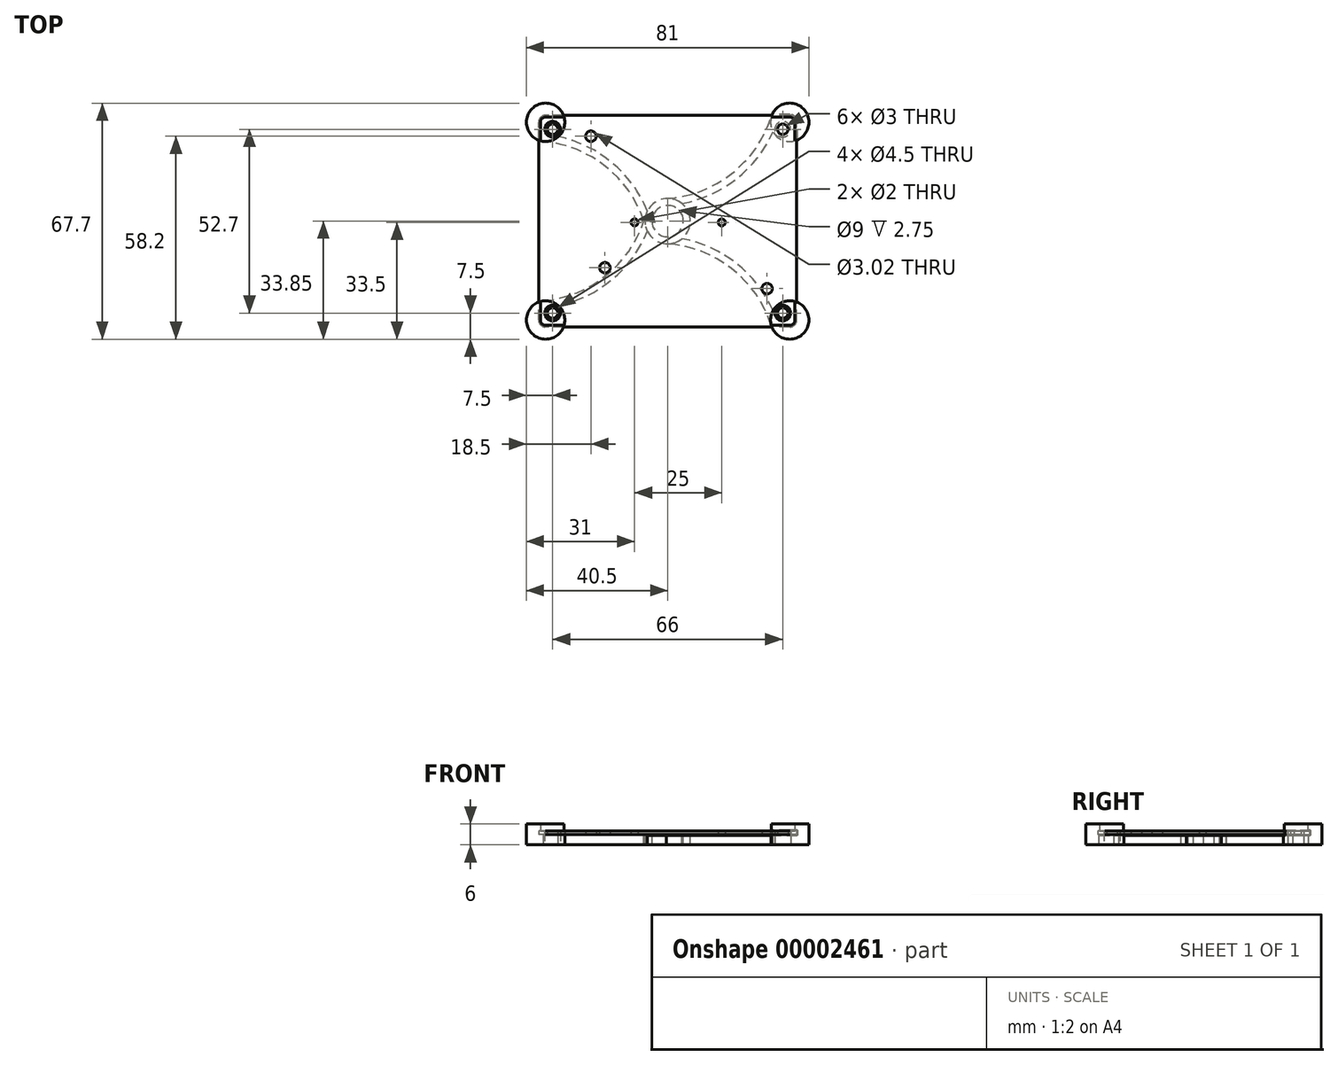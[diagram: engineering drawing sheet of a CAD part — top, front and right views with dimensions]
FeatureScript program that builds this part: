
annotation { "Feature Type Name" : "Feature", "Feature Type Description" : "" }
export const myFeature = defineFeature(function(context is Context, id is Id, definition is map)
    precondition{}
    {
        {
            var Q0;
            Q0=qCreatedBy(makeId("Top.planeOp"),FACE);
            var sketch = newSketch(context, id + "F0", { "sketchPlane" : qUnion([Q0])});
            skLineSegment(sketch, "E0.rect.bottom", {"start": v(35, -30.35) * mm, "end": v(-35, -30.35) * mm});
            skLineSegment(sketch, "E0.rect.top", {"start": v(35, 30.35) * mm, "end": v(-35, 30.35) * mm});
            skLineSegment(sketch, "E0.rect.left", {"start": v(37, -28.35) * mm, "end": v(37, 28.35) * mm});
            skLineSegment(sketch, "E0.rect.right", {"start": v(-37, -28.35) * mm, "end": v(-37, 28.35) * mm});
            skPoint(sketch, "E0.rect.middle", {"position": v(0, 0) * mm});
            skPoint(sketch, "E1.visualSharp", {"position": v(-37, 30.35) * mm});
            skArc(sketch, "E1.filletArc", {"start": v(-35, 30.35) * mm, "mid": v(-36.41, 29.76) * mm, "end": v(-37, 28.35) * mm});
            skPoint(sketch, "E2.visualSharp", {"position": v(37, 30.35) * mm});
            skArc(sketch, "E2.filletArc", {"start": v(37, 28.35) * mm, "mid": v(36.41, 29.76) * mm, "end": v(35, 30.35) * mm});
            skPoint(sketch, "E3.visualSharp", {"position": v(37, -30.35) * mm});
            skArc(sketch, "E3.filletArc", {"start": v(35, -30.35) * mm, "mid": v(36.41, -29.76) * mm, "end": v(37, -28.35) * mm});
            skPoint(sketch, "E4.visualSharp", {"position": v(-37, -30.35) * mm});
            skArc(sketch, "E4.filletArc", {"start": v(-37, -28.35) * mm, "mid": v(-36.41, -29.76) * mm, "end": v(-35, -30.35) * mm});
            skLineSegment(sketch, "E5.rect.bottom", {"start": v(33, -26.35) * mm, "end": v(-33, -26.35) * mm, "construction": true});
            skLineSegment(sketch, "E5.rect.top", {"start": v(33, 26.35) * mm, "end": v(-33, 26.35) * mm, "construction": true});
            skLineSegment(sketch, "E5.rect.left", {"start": v(33, -26.35) * mm, "end": v(33, 26.35) * mm, "construction": true});
            skLineSegment(sketch, "E5.rect.right", {"start": v(-33, -26.35) * mm, "end": v(-33, 26.35) * mm, "construction": true});
            skCircle(sketch, "E6", {"center": v(-33, 26.35) * mm, "radius": 1.5 * mm});
            skCircle(sketch, "E7", {"center": v(33, 26.35) * mm, "radius": 1.5 * mm});
            skCircle(sketch, "E8", {"center": v(33, -26.35) * mm, "radius": 1.5 * mm});
            skCircle(sketch, "E9", {"center": v(-33, -26.35) * mm, "radius": 1.5 * mm});
            skLineSegment(sketch, "E10", {"start": v(-33, 26.35) * mm, "end": v(0, 0) * mm, "construction": true});
            skLineSegment(sketch, "E11", {"start": v(33, 26.35) * mm, "end": v(0, 0) * mm, "construction": true});
            skCircle(sketch, "E12", {"center": v(-22, 24.35) * mm, "radius": 1.51 * mm});
            skCircle(sketch, "E13", {"center": v(-18, -13.35) * mm, "radius": 1.5 * mm});
            skCircle(sketch, "E14", {"center": v(28.5, -19.35) * mm, "radius": 1.5 * mm});
            skCircle(sketch, "E15", {"center": v(15.5, -0.35) * mm, "radius": 1 * mm});
            skCircle(sketch, "E16", {"center": v(-9.5, -0.35) * mm, "radius": 1 * mm});
            skCircle(sketch, "E17", {"center": v(-33, 26.35) * mm, "radius": 5.5 * mm, "construction": true});
            skCircle(sketch, "E18", {"center": v(33, 26.35) * mm, "radius": 5.5 * mm, "construction": true});
            skSolve(sketch);
        }
        {
            var Q0;
            Q0=qSketchRegion(id+"F0",true);
            extrude(context, id + "F1", {"entities" : qUnion([Q0]), "depth" : 1 * mm});
        }
        {
            var Q0;
            Q0=qCreatedBy(makeId("Top.planeOp"),FACE);
            var sketch = newSketch(context, id + "F2", { "sketchPlane" : qUnion([Q0])});
            skCircle(sketch, "E19", {"center": v(0, 0) * mm, "radius": 4.5 * mm});
            skLineSegment(sketch, "E20", {"start": v(0, 30.35) * mm, "end": v(0, -30.35) * mm, "construction": true});
            skCircle(sketch, "E21.0", {"center": v(0, 0) * mm, "radius": 6.5 * mm});
            skSolve(sketch);
        }
        {
            var Q0;
            Q0=qSketchRegion(id+"F2",true);
            extrude(context, id + "F3", {"entities" : qUnion([Q0]), "oppositeDirection" : true, "depth" : 3 * mm});
        }
        {
            var Q0;
            Q0=qCreatedBy(makeId("Top.planeOp"),FACE);
            cPlane(context, id + "F4", {"entities" : qUnion([Q0]), "cplaneType" : CPlaneType.OFFSET, "offset" : 13 * mm, "oppositeDirection" : true, "width" : 150 * mm, "height" : 150 * mm});
        }
        {
            var Q0;
            Q0=qCreatedBy(id+"F4.planeOp",FACE);
            var sketch = newSketch(context, id + "F5", { "sketchPlane" : qUnion([Q0])});
            skCircle(sketch, "E22", {"center": v(33, 26.35) * mm, "radius": 2.25 * mm});
            skCircle(sketch, "E23", {"center": v(35, 28.35) * mm, "radius": 5.5 * mm});
            skSolve(sketch);
        }
        {
            var Q0;
            Q0=qSketchRegion(id+"F5",true);
            extrude(context, id + "F6", {"entities" : qUnion([Q0]), "operationType" : NewBodyOperationType.ADD, "depth" : 6 * mm});
        }
        {
            var Q0;
            Q0=makeQuery(id+"F6.opExtrude","SWEPT_BODY",BODY,{"disambiguationData":[OSD([sQuery(id+"F5.wireOp",EDGE,"E22"),sQuery(id+"F5.wireOp",EDGE,"E23")])]});
            transform(context, id + "F7", {"entities" : qUnion([Q0]), "transformType" : TransformType.TRANSLATION_3D, "dx" : 0 * mm, "dy" : 0 * mm, "dz" : 10 * mm, "makeCopy" : false});
        }
        {
            var Q0;
            Q0=makeQuery(id+"F1.opExtrude","CAP_FACE",FACE,{"disambiguationData":[OSD([sQuery(id+"F0.wireOp",EDGE,"E0.rect.bottom"),sQuery(id+"F0.wireOp",EDGE,"E0.rect.top"),sQuery(id+"F0.wireOp",EDGE,"E0.rect.left"),sQuery(id+"F0.wireOp",EDGE,"E0.rect.right"),sQuery(id+"F0.wireOp",EDGE,"E1.filletArc"),sQuery(id+"F0.wireOp",EDGE,"E2.filletArc"),sQuery(id+"F0.wireOp",EDGE,"E3.filletArc"),sQuery(id+"F0.wireOp",EDGE,"E4.filletArc"),sQuery(id+"F0.wireOp",EDGE,"E6"),sQuery(id+"F0.wireOp",EDGE,"E7"),sQuery(id+"F0.wireOp",EDGE,"E8"),sQuery(id+"F0.wireOp",EDGE,"E9"),sQuery(id+"F0.wireOp",EDGE,"E12"),sQuery(id+"F0.wireOp",EDGE,"E13"),sQuery(id+"F0.wireOp",EDGE,"E14"),sQuery(id+"F0.wireOp",EDGE,"E15"),sQuery(id+"F0.wireOp",EDGE,"E16")])],"isStart":true});
            var sketch = newSketch(context, id + "F8", { "sketchPlane" : qUnion([Q0])});
            skCircle(sketch, "E24", {"center": v(35, -28.35) * mm, "radius": 5.5 * mm, "construction": true});
            skCircle(sketch, "E25", {"center": v(0, 0) * mm, "radius": 6.5 * mm, "construction": true});
            skArc(sketch, "E26", {"start": v(6.26, 1.75) * mm, "mid": v(17.1, -15.09) * mm, "end": v(35.55, -22.88) * mm, "construction": true});
            skArc(sketch, "E27.0", {"start": v(5.78, -2.97) * mm, "mid": v(15.95, -16.74) * mm, "end": v(31.35, -24.24) * mm, "construction": true});
            skArc(sketch, "E28", {"start": v(35.55, -22.88) * mm, "mid": v(33.3, -23.12) * mm, "end": v(31.35, -24.24) * mm, "construction": true});
            skArc(sketch, "E29", {"start": v(5.78, -2.97) * mm, "mid": v(6.47, -0.65) * mm, "end": v(6.26, 1.75) * mm, "construction": true});
            skLineSegment(sketch, "E30", {"start": v(0, 0) * mm, "end": v(0, -33.77) * mm, "construction": true});
            skLineSegment(sketch, "E31", {"start": v(0, 0) * mm, "end": v(35, -28.35) * mm, "construction": true});
            skArc(sketch, "E32.0.MirrorCS", {"start": v(-0.4, -6.49) * mm, "mid": v(18.31, -13.6) * mm, "end": v(29.76, -30.02) * mm});
            skArc(sketch, "E32.1.MirrorCS", {"start": v(4.1, -5.04) * mm, "mid": v(1.98, -6.19) * mm, "end": v(-0.4, -6.49) * mm});
            skArc(sketch, "E32.2.MirrorCS", {"start": v(29.76, -30.02) * mm, "mid": v(29.53, -27.78) * mm, "end": v(30.22, -25.63) * mm});
            skArc(sketch, "E32.3.MirrorCS", {"start": v(4.1, -5.04) * mm, "mid": v(19.69, -12.13) * mm, "end": v(30.22, -25.63) * mm});
            skLineSegment(sketch, "E33", {"start": v(0, 0) * mm, "end": v(47.85, 0) * mm, "construction": true});
            skArc(sketch, "E34.2.MirrorCS", {"start": v(29.76, -30.02) * mm, "mid": v(29.53, -27.78) * mm, "end": v(30.22, -25.63) * mm, "construction": true});
            skArc(sketch, "E34.4.MirrorCS", {"start": v(-0.4, -6.49) * mm, "mid": v(18.31, -13.6) * mm, "end": v(29.76, -30.02) * mm, "construction": true});
            skArc(sketch, "E34.5.MirrorCS", {"start": v(4.1, -5.04) * mm, "mid": v(19.69, -12.13) * mm, "end": v(30.22, -25.63) * mm, "construction": true});
            skArc(sketch, "E34.6.MirrorCS", {"start": v(4.1, -5.04) * mm, "mid": v(1.98, -6.19) * mm, "end": v(-0.4, -6.49) * mm, "construction": true});
            skArc(sketch, "E35.4.MirrorCS", {"start": v(5.78, 2.97) * mm, "mid": v(15.95, 16.74) * mm, "end": v(31.35, 24.24) * mm, "construction": true});
            skArc(sketch, "E35.5.MirrorCS", {"start": v(4.1, 5.04) * mm, "mid": v(1.98, 6.19) * mm, "end": v(-0.4, 6.49) * mm, "construction": true});
            skArc(sketch, "E35.6.MirrorCS", {"start": v(-0.4, 6.49) * mm, "mid": v(18.31, 13.6) * mm, "end": v(29.76, 30.02) * mm, "construction": true});
            skArc(sketch, "E35.7.MirrorCS", {"start": v(6.26, -1.75) * mm, "mid": v(17.1, 15.09) * mm, "end": v(35.55, 22.88) * mm, "construction": true});
            skArc(sketch, "E35.8.MirrorCS", {"start": v(35.55, 22.88) * mm, "mid": v(33.3, 23.12) * mm, "end": v(31.35, 24.24) * mm, "construction": true});
            skArc(sketch, "E35.9.MirrorCS", {"start": v(4.1, 5.04) * mm, "mid": v(19.69, 12.13) * mm, "end": v(30.22, 25.63) * mm, "construction": true});
            skArc(sketch, "E35.10.MirrorCS", {"start": v(5.78, 2.97) * mm, "mid": v(6.47, 0.65) * mm, "end": v(6.26, -1.75) * mm, "construction": true});
            skArc(sketch, "E35.11.MirrorCS", {"start": v(29.76, 30.02) * mm, "mid": v(29.53, 27.78) * mm, "end": v(30.22, 25.63) * mm, "construction": true});
            skArc(sketch, "E35.12.MirrorCS", {"start": v(35.55, 22.88) * mm, "mid": v(33.3, 23.12) * mm, "end": v(31.35, 24.24) * mm, "construction": true});
            skArc(sketch, "E35.13.MirrorCS", {"start": v(29.76, 30.02) * mm, "mid": v(29.53, 27.78) * mm, "end": v(30.22, 25.63) * mm});
            skArc(sketch, "E35.14.MirrorCS", {"start": v(5.78, 2.97) * mm, "mid": v(15.95, 16.74) * mm, "end": v(31.35, 24.24) * mm, "construction": true});
            skArc(sketch, "E35.15.MirrorCS", {"start": v(-0.4, 6.49) * mm, "mid": v(18.31, 13.6) * mm, "end": v(29.76, 30.02) * mm});
            skArc(sketch, "E35.16.MirrorCS", {"start": v(5.78, 2.97) * mm, "mid": v(6.47, 0.65) * mm, "end": v(6.26, -1.75) * mm, "construction": true});
            skArc(sketch, "E35.17.MirrorCS", {"start": v(4.1, 5.04) * mm, "mid": v(1.98, 6.19) * mm, "end": v(-0.4, 6.49) * mm});
            skArc(sketch, "E35.18.MirrorCS", {"start": v(6.26, -1.75) * mm, "mid": v(17.1, 15.09) * mm, "end": v(35.55, 22.88) * mm, "construction": true});
            skArc(sketch, "E35.19.MirrorCS", {"start": v(4.1, 5.04) * mm, "mid": v(19.69, 12.13) * mm, "end": v(30.22, 25.63) * mm});
            skArc(sketch, "E36.0.MirrorCS", {"start": v(-35.55, 22.88) * mm, "mid": v(-33.3, 23.12) * mm, "end": v(-31.35, 24.24) * mm});
            skArc(sketch, "E36.1.MirrorCS", {"start": v(-35.55, -22.88) * mm, "mid": v(-33.3, -23.12) * mm, "end": v(-31.35, -24.24) * mm});
            skArc(sketch, "E36.2.MirrorCS", {"start": v(-5.78, 2.97) * mm, "mid": v(-6.47, 0.65) * mm, "end": v(-6.26, -1.75) * mm});
            skArc(sketch, "E36.3.MirrorCS", {"start": v(-5.78, 2.97) * mm, "mid": v(-15.95, 16.74) * mm, "end": v(-31.35, 24.24) * mm});
            skArc(sketch, "E36.4.MirrorCS", {"start": v(-6.26, -1.75) * mm, "mid": v(-17.1, 15.09) * mm, "end": v(-35.55, 22.88) * mm});
            skArc(sketch, "E36.5.MirrorCS", {"start": v(-6.26, 1.75) * mm, "mid": v(-17.1, -15.09) * mm, "end": v(-35.55, -22.88) * mm});
            skArc(sketch, "E36.6.MirrorCS", {"start": v(-5.78, -2.97) * mm, "mid": v(-6.47, -0.65) * mm, "end": v(-6.26, 1.75) * mm});
            skArc(sketch, "E36.7.MirrorCS", {"start": v(-5.78, -2.97) * mm, "mid": v(-15.95, -16.74) * mm, "end": v(-31.35, -24.24) * mm});
            skSolve(sketch);
        }
        {
            var Q0;
            Q0=qSketchRegion(id+"F8",true);
            extrude(context, id + "F9", {"entities" : qUnion([Q0]), "depth" : 3 * mm});
        }
        {
            var Q0;
            Q0=makeQuery(id+"F1.opExtrude","CAP_FACE",FACE,{"disambiguationData":[OSD([sQuery(id+"F0.wireOp",EDGE,"E0.rect.bottom"),sQuery(id+"F0.wireOp",EDGE,"E0.rect.top"),sQuery(id+"F0.wireOp",EDGE,"E0.rect.left"),sQuery(id+"F0.wireOp",EDGE,"E0.rect.right"),sQuery(id+"F0.wireOp",EDGE,"E1.filletArc"),sQuery(id+"F0.wireOp",EDGE,"E2.filletArc"),sQuery(id+"F0.wireOp",EDGE,"E3.filletArc"),sQuery(id+"F0.wireOp",EDGE,"E4.filletArc"),sQuery(id+"F0.wireOp",EDGE,"E6"),sQuery(id+"F0.wireOp",EDGE,"E7"),sQuery(id+"F0.wireOp",EDGE,"E8"),sQuery(id+"F0.wireOp",EDGE,"E9"),sQuery(id+"F0.wireOp",EDGE,"E12"),sQuery(id+"F0.wireOp",EDGE,"E13"),sQuery(id+"F0.wireOp",EDGE,"E14"),sQuery(id+"F0.wireOp",EDGE,"E15"),sQuery(id+"F0.wireOp",EDGE,"E16")])],"isStart":false});
            var sketch = newSketch(context, id + "F10", { "sketchPlane" : qUnion([Q0])});
            skLineSegment(sketch, "E37.0", {"start": v(35, 29.85) * mm, "end": v(25, 29.85) * mm});
            skArc(sketch, "E38.0", {"start": v(36.5, 28.35) * mm, "mid": v(36.06, 29.41) * mm, "end": v(35, 29.85) * mm});
            skLineSegment(sketch, "E39.0", {"start": v(36.5, 18.35) * mm, "end": v(36.5, 28.35) * mm});
            skLineSegment(sketch, "E40", {"start": v(25, 29.85) * mm, "end": v(25, 18.35) * mm});
            skLineSegment(sketch, "E41", {"start": v(25, 18.35) * mm, "end": v(36.5, 18.35) * mm});
            skSolve(sketch);
        }
        {
            var Q0;
            Q0=qSketchRegion(id+"F10",true);
            var Q1;
            Q1=makeQuery(id+"F6.opExtrude","CAP_FACE",FACE,{"disambiguationData":[OSD([sQuery(id+"F5.wireOp",EDGE,"E22"),sQuery(id+"F5.wireOp",EDGE,"E23")])],"isStart":false});
            extrude(context, id + "F11", {"entities" : qUnion([Q0]), "operationType" : NewBodyOperationType.REMOVE, "endBound" : BoundingType.UP_TO_SURFACE, "endBoundEntityFace" : qUnion([Q1]), "depth" : 25 * mm});
        }
        {
            var Q0;
            Q0=makeQuery(id+"F6.opExtrude","SWEPT_BODY",BODY,{"disambiguationData":[OSD([sQuery(id+"F5.wireOp",EDGE,"E22"),sQuery(id+"F5.wireOp",EDGE,"E23")])]});
            transform(context, id + "F12", {"entities" : qUnion([Q0]), "transformType" : TransformType.TRANSLATION_3D, "dx" : -(66 * mm), "dy" : 0 * mm, "dz" : 0 * mm, "makeCopy" : true});
        }
        {
            var Q0;
            Q0=makeQuery(id+"F12.opPattern","COPY",BODY,{"derivedFrom":makeQuery(id+"F6.opExtrude","SWEPT_BODY",BODY,{"disambiguationData":[OSD([sQuery(id+"F5.wireOp",EDGE,"E22"),sQuery(id+"F5.wireOp",EDGE,"E23")])]}),"instanceName":"1"});
            var Q1;
            Q1=makeQuery(id+"F12.opPattern","COPY",EDGE,{"derivedFrom":makeQuery(id+"F6.opExtrude","CAP_EDGE",EDGE,{"disambiguationData":[OSD([sQuery(id+"F5.wireOp",EDGE,"E22")])],"isStart":true}),"instanceName":"1"});
            transform(context, id + "F13", {"entities" : qUnion([Q0]), "transformType" : TransformType.ROTATION, "transformAxis" : qUnion([Q1]), "angle" : 90 * degree, "oppositeX" : false, "oppositeY" : false, "oppositeZ" : false, "makeCopy" : false});
        }
        {
            var Q0;
            Q0=makeQuery(id+"F6.opExtrude","SWEPT_BODY",BODY,{"disambiguationData":[OSD([sQuery(id+"F5.wireOp",EDGE,"E22"),sQuery(id+"F5.wireOp",EDGE,"E23")])]});
            transform(context, id + "F14", {"entities" : qUnion([Q0]), "transformType" : TransformType.TRANSLATION_3D, "dx" : -(66 * mm), "dy" : -(52.7 * mm), "dz" : 0 * mm, "makeCopy" : true});
        }
        {
            var Q0;
            Q0=makeQuery(id+"F14.opPattern","COPY",BODY,{"derivedFrom":makeQuery(id+"F6.opExtrude","SWEPT_BODY",BODY,{"disambiguationData":[OSD([sQuery(id+"F5.wireOp",EDGE,"E22"),sQuery(id+"F5.wireOp",EDGE,"E23")])]}),"instanceName":"1"});
            var Q1;
            Q1=makeQuery(id+"F14.opPattern","COPY",EDGE,{"derivedFrom":makeQuery(id+"F6.opExtrude","CAP_EDGE",EDGE,{"disambiguationData":[OSD([sQuery(id+"F5.wireOp",EDGE,"E22")])],"isStart":true}),"instanceName":"1"});
            transform(context, id + "F15", {"entities" : qUnion([Q0]), "transformType" : TransformType.ROTATION, "transformAxis" : qUnion([Q1]), "angle" : 180 * degree, "oppositeDirection" : true, "oppositeX" : false, "oppositeY" : false, "oppositeZ" : false, "makeCopy" : false});
        }
        {
            var Q0;
            Q0=makeQuery(id+"F6.opExtrude","SWEPT_BODY",BODY,{"disambiguationData":[OSD([sQuery(id+"F5.wireOp",EDGE,"E22"),sQuery(id+"F5.wireOp",EDGE,"E23")])]});
            transform(context, id + "F16", {"entities" : qUnion([Q0]), "transformType" : TransformType.TRANSLATION_3D, "dx" : 0 * mm, "dy" : -(52.7 * mm), "dz" : 0 * mm, "makeCopy" : true});
        }
        {
            var Q0;
            Q0=makeQuery(id+"F16.opPattern","COPY",BODY,{"derivedFrom":makeQuery(id+"F6.opExtrude","SWEPT_BODY",BODY,{"disambiguationData":[OSD([sQuery(id+"F5.wireOp",EDGE,"E22"),sQuery(id+"F5.wireOp",EDGE,"E23")])]}),"instanceName":"1"});
            var Q1;
            Q1=makeQuery(id+"F16.opPattern","COPY",EDGE,{"derivedFrom":makeQuery(id+"F6.opExtrude","CAP_EDGE",EDGE,{"disambiguationData":[OSD([sQuery(id+"F5.wireOp",EDGE,"E22")])],"isStart":true}),"instanceName":"1"});
            transform(context, id + "F17", {"entities" : qUnion([Q0]), "transformType" : TransformType.ROTATION, "transformAxis" : qUnion([Q1]), "angle" : 90 * degree, "oppositeDirection" : true, "oppositeX" : false, "oppositeY" : false, "oppositeZ" : false, "makeCopy" : false});
        }
        {
            var Q0;
            Q0=makeQuery(id+"F1.opExtrude","SWEPT_BODY",BODY,{"disambiguationData":[OSD([sQuery(id+"F0.wireOp",EDGE,"E0.rect.bottom"),sQuery(id+"F0.wireOp",EDGE,"E0.rect.top"),sQuery(id+"F0.wireOp",EDGE,"E0.rect.left"),sQuery(id+"F0.wireOp",EDGE,"E0.rect.right"),sQuery(id+"F0.wireOp",EDGE,"E1.filletArc"),sQuery(id+"F0.wireOp",EDGE,"E2.filletArc"),sQuery(id+"F0.wireOp",EDGE,"E3.filletArc"),sQuery(id+"F0.wireOp",EDGE,"E4.filletArc"),sQuery(id+"F0.wireOp",EDGE,"E6"),sQuery(id+"F0.wireOp",EDGE,"E7"),sQuery(id+"F0.wireOp",EDGE,"E8"),sQuery(id+"F0.wireOp",EDGE,"E9"),sQuery(id+"F0.wireOp",EDGE,"E12"),sQuery(id+"F0.wireOp",EDGE,"E13"),sQuery(id+"F0.wireOp",EDGE,"E14"),sQuery(id+"F0.wireOp",EDGE,"E15"),sQuery(id+"F0.wireOp",EDGE,"E16")])]});
            var Q1;
            Q1=makeQuery(id+"F6.opExtrude","SWEPT_BODY",BODY,{"disambiguationData":[OSD([sQuery(id+"F5.wireOp",EDGE,"E22"),sQuery(id+"F5.wireOp",EDGE,"E23")])]});
            var Q2;
            Q2=makeQuery(id+"F3.opExtrude","SWEPT_BODY",BODY,{"disambiguationData":[OSD([sQuery(id+"F2.wireOp",EDGE,"E19"),sQuery(id+"F2.wireOp",EDGE,"E21.0")])]});
            var Q3;
            Q3=makeQuery(id+"F9.opExtrude","SWEPT_BODY",BODY,{"disambiguationData":[OSD([sQuery(id+"F8.wireOp",EDGE,"E26"),sQuery(id+"F8.wireOp",EDGE,"E27.0"),sQuery(id+"F8.wireOp",EDGE,"E28"),sQuery(id+"F8.wireOp",EDGE,"E29")])]});
            var Q4;
            Q4=makeQuery(id+"F9.opExtrude","SWEPT_BODY",BODY,{"disambiguationData":[OSD([sQuery(id+"F8.wireOp",EDGE,"E32.0.MirrorCS"),sQuery(id+"F8.wireOp",EDGE,"E32.1.MirrorCS"),sQuery(id+"F8.wireOp",EDGE,"E32.2.MirrorCS"),sQuery(id+"F8.wireOp",EDGE,"E32.3.MirrorCS")])]});
            var Q5;
            Q5=makeQuery(id+"F9.opExtrude","SWEPT_BODY",BODY,{"disambiguationData":[OSD([sQuery(id+"F8.wireOp",EDGE,"E35.13.MirrorCS"),sQuery(id+"F8.wireOp",EDGE,"E35.15.MirrorCS"),sQuery(id+"F8.wireOp",EDGE,"E35.17.MirrorCS"),sQuery(id+"F8.wireOp",EDGE,"E35.19.MirrorCS")])]});
            var Q6;
            Q6=makeQuery(id+"F1.opExtrude","CAP_FACE",FACE,{"disambiguationData":[OSD([sQuery(id+"F0.wireOp",EDGE,"E0.rect.bottom"),sQuery(id+"F0.wireOp",EDGE,"E0.rect.top"),sQuery(id+"F0.wireOp",EDGE,"E0.rect.left"),sQuery(id+"F0.wireOp",EDGE,"E0.rect.right"),sQuery(id+"F0.wireOp",EDGE,"E1.filletArc"),sQuery(id+"F0.wireOp",EDGE,"E2.filletArc"),sQuery(id+"F0.wireOp",EDGE,"E3.filletArc"),sQuery(id+"F0.wireOp",EDGE,"E4.filletArc"),sQuery(id+"F0.wireOp",EDGE,"E6"),sQuery(id+"F0.wireOp",EDGE,"E7"),sQuery(id+"F0.wireOp",EDGE,"E8"),sQuery(id+"F0.wireOp",EDGE,"E9"),sQuery(id+"F0.wireOp",EDGE,"E12"),sQuery(id+"F0.wireOp",EDGE,"E13"),sQuery(id+"F0.wireOp",EDGE,"E14"),sQuery(id+"F0.wireOp",EDGE,"E15"),sQuery(id+"F0.wireOp",EDGE,"E16")])],"isStart":false});
            var Q7;
            Q7=makeQuery(id+"F1.opExtrude","SWEPT_FACE",FACE,{"disambiguationData":[OSD([sQuery(id+"F0.wireOp",EDGE,"E0.rect.top")])]});
            var Q8;
            Q8=makeQuery(id+"F1.opExtrude","SWEPT_FACE",FACE,{"disambiguationData":[OSD([sQuery(id+"F0.wireOp",EDGE,"E0.rect.left")])]});
            var Q9;
            Q9=makeQuery(id+"F1.opExtrude","CAP_FACE",FACE,{"disambiguationData":[OSD([sQuery(id+"F0.wireOp",EDGE,"E0.rect.bottom"),sQuery(id+"F0.wireOp",EDGE,"E0.rect.top"),sQuery(id+"F0.wireOp",EDGE,"E0.rect.left"),sQuery(id+"F0.wireOp",EDGE,"E0.rect.right"),sQuery(id+"F0.wireOp",EDGE,"E1.filletArc"),sQuery(id+"F0.wireOp",EDGE,"E2.filletArc"),sQuery(id+"F0.wireOp",EDGE,"E3.filletArc"),sQuery(id+"F0.wireOp",EDGE,"E4.filletArc"),sQuery(id+"F0.wireOp",EDGE,"E6"),sQuery(id+"F0.wireOp",EDGE,"E7"),sQuery(id+"F0.wireOp",EDGE,"E8"),sQuery(id+"F0.wireOp",EDGE,"E9"),sQuery(id+"F0.wireOp",EDGE,"E12"),sQuery(id+"F0.wireOp",EDGE,"E13"),sQuery(id+"F0.wireOp",EDGE,"E14"),sQuery(id+"F0.wireOp",EDGE,"E15"),sQuery(id+"F0.wireOp",EDGE,"E16")])],"isStart":true});
            var Q10;
            Q10=makeQuery(id+"F1.opExtrude","SWEPT_FACE",FACE,{"disambiguationData":[OSD([sQuery(id+"F0.wireOp",EDGE,"E2.filletArc")])]});
            booleanBodies(context, id + "F18", {"operationType" : BooleanOperationType.SUBTRACTION, "tools" : qUnion([Q0]), "targets" : qUnion([Q1, Q2, Q3, Q4, Q5]), "offset" : true, "entitiesToOffset" : qUnion([Q6, Q7, Q8, Q9, Q10]), "offsetDistance" : 0.25 * mm, "keepTools" : true, "reFillet" : true});
        }
    });
